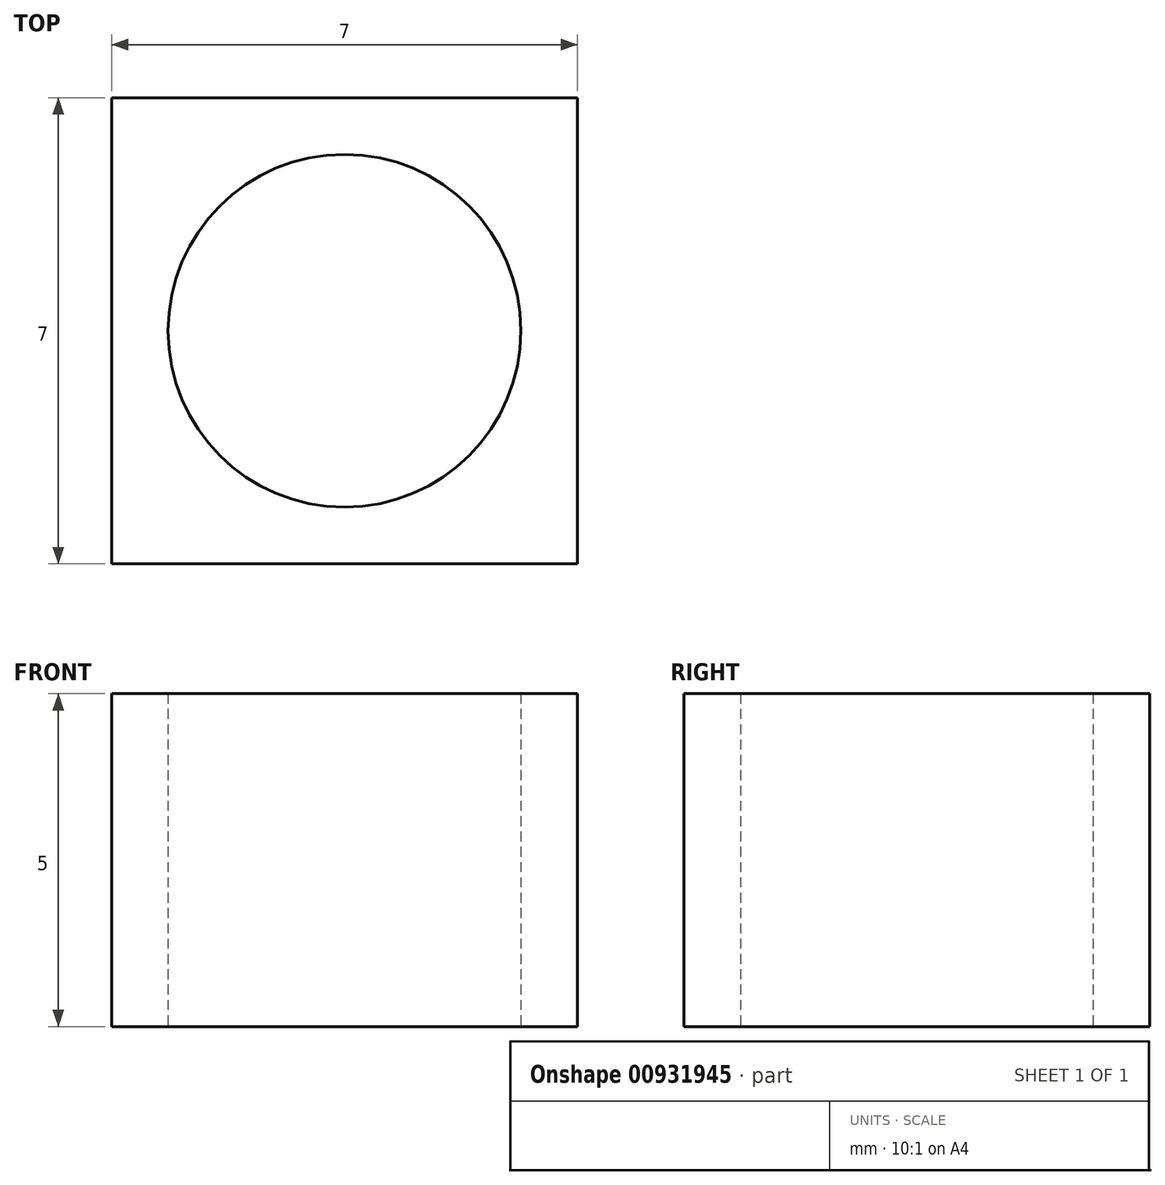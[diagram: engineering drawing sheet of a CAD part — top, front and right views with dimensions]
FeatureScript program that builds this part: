
annotation { "Feature Type Name" : "Feature", "Feature Type Description" : "" }
export const myFeature = defineFeature(function(context is Context, id is Id, definition is map)
    precondition{}
    {
        {
            var Q0;
            Q0=qCreatedBy(makeId("Top.planeOp"),FACE);
            var sketch = newSketch(context, id + "F0", { "sketchPlane" : qUnion([Q0])});
            skCircle(sketch, "E0", {"center": v(0, 0) * mm, "radius": 2.65 * mm});
            skLineSegment(sketch, "E1.bottom", {"start": v(3.5, 3.5) * mm, "end": v(-3.5, 3.5) * mm});
            skLineSegment(sketch, "E1.top", {"start": v(3.5, -3.5) * mm, "end": v(-3.5, -3.5) * mm});
            skLineSegment(sketch, "E1.left", {"start": v(3.5, 3.5) * mm, "end": v(3.5, -3.5) * mm});
            skLineSegment(sketch, "E1.right", {"start": v(-3.5, 3.5) * mm, "end": v(-3.5, -3.5) * mm});
            skSolve(sketch);
        }
        {
            var Q0;
            Q0 = qSketchRegion(id + "F0", true);
            extrude(context, id + "F1", {"entities" : qUnion([Q0]), "depth" : 5 * mm, "offsetDistance" : 25.4 * mm});
        }
    });
